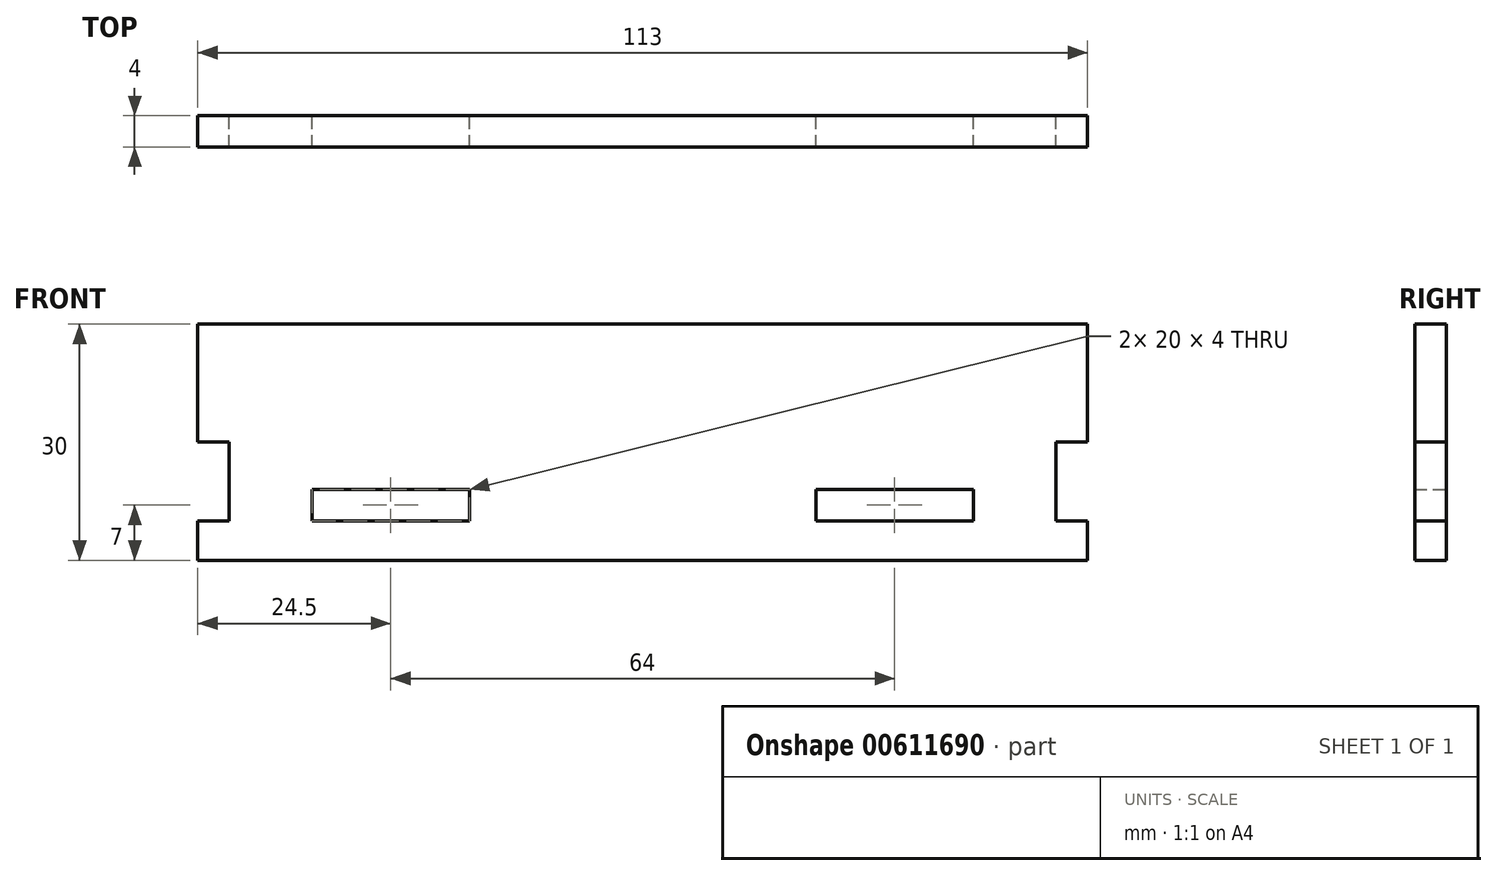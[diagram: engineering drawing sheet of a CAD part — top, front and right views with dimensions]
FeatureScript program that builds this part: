
annotation { "Feature Type Name" : "Feature", "Feature Type Description" : "" }
export const myFeature = defineFeature(function(context is Context, id is Id, definition is map)
    precondition{}
    {
        {
            var Q0;
            Q0=qCreatedBy(makeId("Front.planeOp"),FACE);
            var sketch = newSketch(context, id + "F0", { "sketchPlane" : qUnion([Q0])});
            skLineSegment(sketch, "E0.bottom", {"start": v(56.5, 15) * mm, "end": v(-56.5, 15) * mm});
            skLineSegment(sketch, "E0.top", {"start": v(56.5, -15) * mm, "end": v(-56.5, -15) * mm});
            skLineSegment(sketch, "E0.left", {"start": v(56.5, 15) * mm, "end": v(56.5, 0) * mm});
            skLineSegment(sketch, "E0.right", {"start": v(-56.5, 15) * mm, "end": v(-56.5, 0) * mm});
            skPoint(sketch, "E0.middle", {"position": v(0, 0) * mm});
            skLineSegment(sketch, "E1.bottom", {"start": v(-42, -6) * mm, "end": v(-22, -6) * mm});
            skLineSegment(sketch, "E1.top", {"start": v(-42, -10) * mm, "end": v(-22, -10) * mm});
            skLineSegment(sketch, "E1.left", {"start": v(-42, -6) * mm, "end": v(-42, -10) * mm});
            skLineSegment(sketch, "E1.right", {"start": v(-22, -6) * mm, "end": v(-22, -10) * mm});
            skLineSegment(sketch, "E2.MirrorCS", {"start": v(42, -6) * mm, "end": v(22, -6) * mm});
            skLineSegment(sketch, "E3.MirrorCS", {"start": v(42, -10) * mm, "end": v(22, -10) * mm});
            skLineSegment(sketch, "E4.MirrorCS", {"start": v(42, -6) * mm, "end": v(42, -10) * mm});
            skLineSegment(sketch, "E5.MirrorCS", {"start": v(22, -6) * mm, "end": v(22, -10) * mm});
            skLineSegment(sketch, "E6.bottom", {"start": v(-56.5, 0) * mm, "end": v(-52.5, 0) * mm});
            skLineSegment(sketch, "E6.top", {"start": v(-56.5, -10) * mm, "end": v(-52.5, -10) * mm});
            skLineSegment(sketch, "E6.right", {"start": v(-52.5, 0) * mm, "end": v(-52.5, -10) * mm});
            skLineSegment(sketch, "E7.MirrorCS", {"start": v(56.5, -10) * mm, "end": v(52.5, -10) * mm});
            skLineSegment(sketch, "E8.MirrorCS", {"start": v(52.5, 0) * mm, "end": v(52.5, -10) * mm});
            skLineSegment(sketch, "E9.MirrorCS", {"start": v(56.5, 0) * mm, "end": v(52.5, 0) * mm});
            skLineSegment(sketch, "E10.trimOffspring", {"start": v(-56.5, -10) * mm, "end": v(-56.5, -15) * mm});
            skLineSegment(sketch, "E11.trimOffspring", {"start": v(56.5, -10) * mm, "end": v(56.5, -15) * mm});
            skSolve(sketch);
        }
        {
            var Q0;
            Q0=makeQuery(id+"F0.imprint","IMPRINT",FACE,{"disambiguationData":[TD([[makeQuery(id+"F0.imprint","IMPRINT",EDGE,{"derivedFrom":sQuery(id+"F0.wireOp",EDGE,"E0.bottom")}),1.0]])]});
            extrude(context, id + "F1", {"entities" : qUnion([Q0]), "depth" : 4 * mm, "offsetDistance" : 25 * mm});
        }
    });
